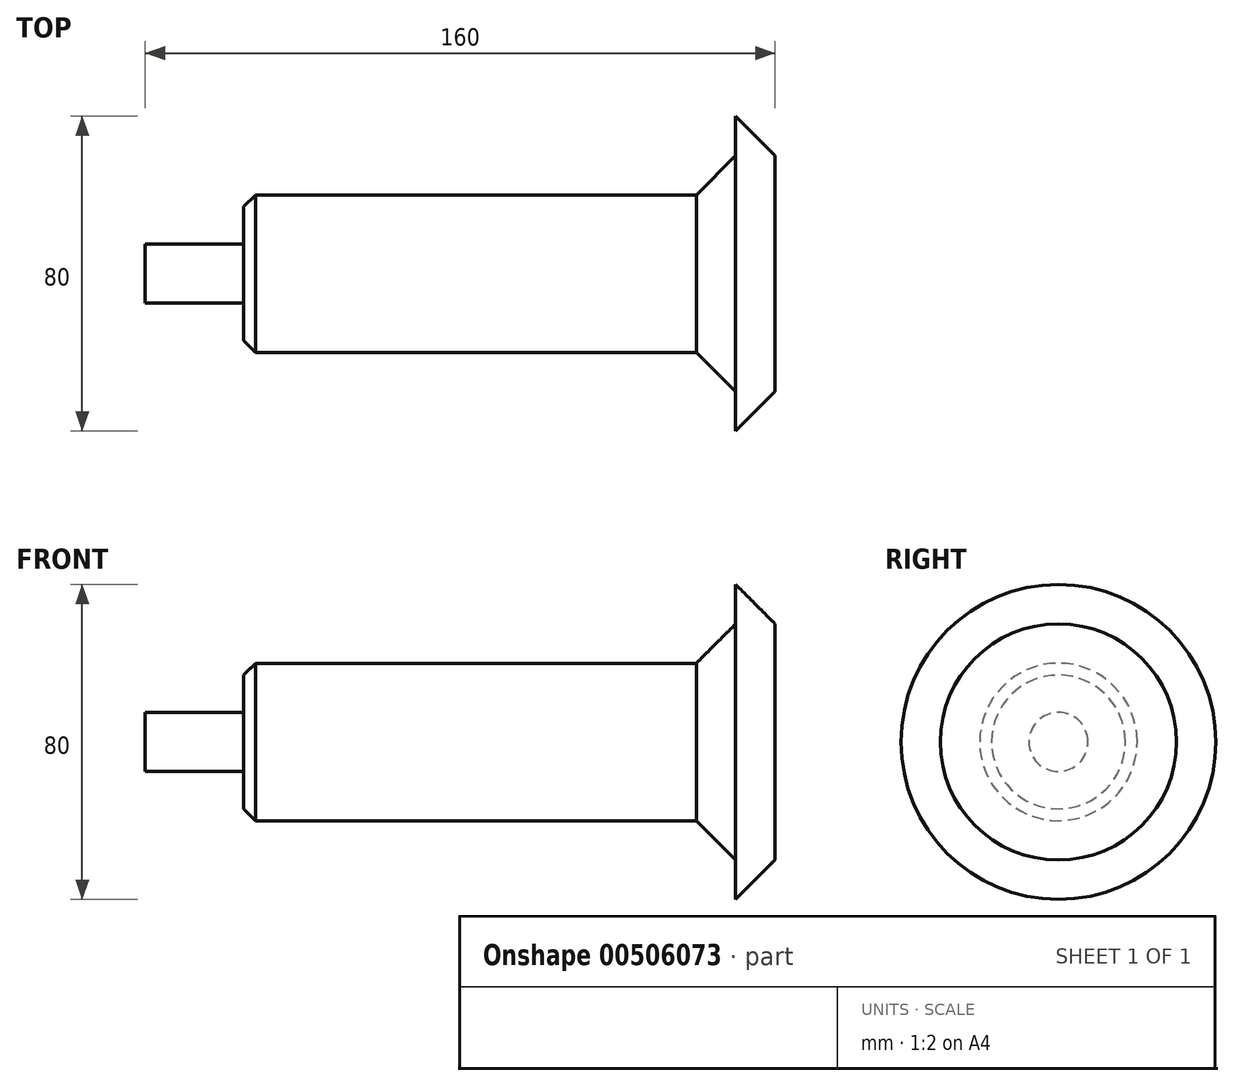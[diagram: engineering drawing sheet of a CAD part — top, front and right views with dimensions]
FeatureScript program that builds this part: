
annotation { "Feature Type Name" : "Feature", "Feature Type Description" : "" }
export const myFeature = defineFeature(function(context is Context, id is Id, definition is map)
    precondition{}
    {
        {
            var Q0;
            Q0=qCreatedBy(makeId("Front.planeOp"),FACE);
            var sketch = newSketch(context, id + "F0", { "sketchPlane" : qUnion([Q0])});
            skLineSegment(sketch, "E0", {"start": v(-75.35, 0) * mm, "end": v(84.65, 0) * mm});
            skLineSegment(sketch, "E1", {"start": v(-75.35, 0) * mm, "end": v(-75.35, 7.5) * mm});
            skLineSegment(sketch, "E2", {"start": v(-75.35, 7.5) * mm, "end": v(-50.35, 7.5) * mm});
            skLineSegment(sketch, "E3", {"start": v(-50.35, 7.5) * mm, "end": v(-50.35, 20) * mm});
            skLineSegment(sketch, "E4", {"start": v(-50.35, 20) * mm, "end": v(64.65, 20) * mm});
            skLineSegment(sketch, "E5", {"start": v(74.65, 30) * mm, "end": v(64.65, 20) * mm});
            skLineSegment(sketch, "E6", {"start": v(74.65, 30) * mm, "end": v(74.65, 40) * mm});
            skLineSegment(sketch, "E7", {"start": v(74.65, 40) * mm, "end": v(84.65, 30) * mm});
            skLineSegment(sketch, "E8", {"start": v(84.65, 30) * mm, "end": v(84.65, 0) * mm});
            skSolve(sketch);
        }
        {
            var Q0;
            Q0=makeQuery(id+"F0.imprint","IMPRINT",FACE,{"disambiguationData":[TD([[makeQuery(id+"F0.imprint","IMPRINT",EDGE,{"derivedFrom":sQuery(id+"F0.wireOp",EDGE,"E0")}),1.0]])]});
            var Q1;
            Q1=sQuery(id+"F0.wireOp",EDGE,"E0");
            revolve(context, id + "F1", {"entities" : qUnion([Q0]), "axis" : qUnion([Q1]), "revolveType" : RevolveType.FULL});
        }
        {
            var Q0;
            Q0=makeQuery(id+"F1.opRevolve","SWEPT_EDGE",EDGE,{"disambiguationData":[OSD([sQuery(id+"F0.wireOp",EDGE,"E3"),sQuery(id+"F0.wireOp",EDGE,"E4")])]});
            chamfer(context, id + "F2", {"entities" : qUnion([Q0]), "width" : 3 * mm, "tangentPropagation" : true});
        }
    });
